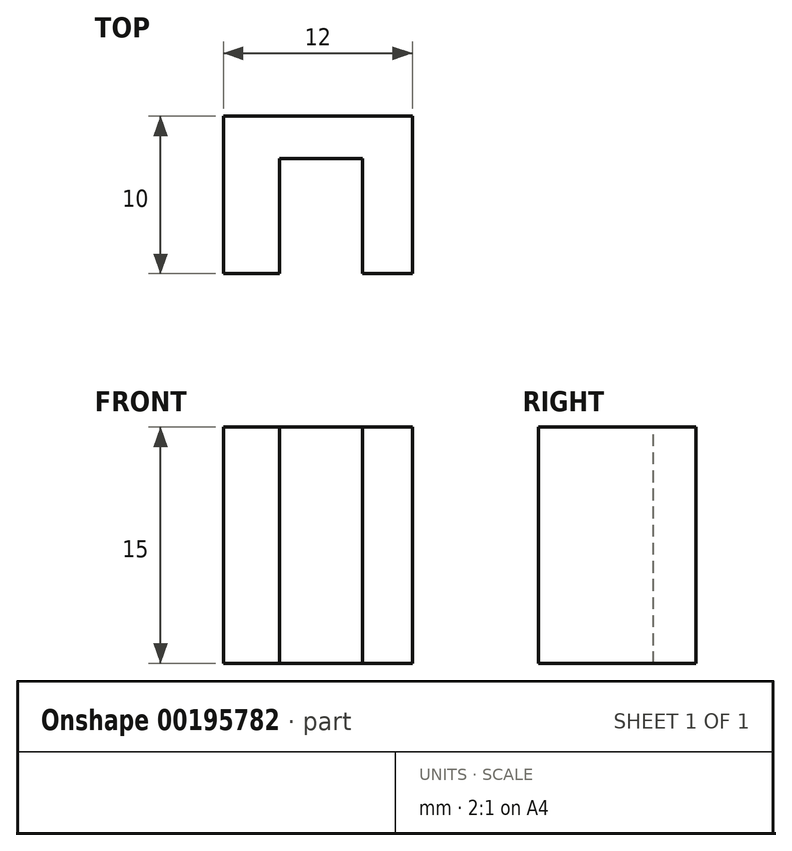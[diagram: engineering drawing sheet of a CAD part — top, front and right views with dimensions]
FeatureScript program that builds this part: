
annotation { "Feature Type Name" : "Feature", "Feature Type Description" : "" }
export const myFeature = defineFeature(function(context is Context, id is Id, definition is map)
    precondition{}
    {
        {
            var Q0;
            Q0=qCreatedBy(makeId("Top.planeOp"),FACE);
            var sketch = newSketch(context, id + "F0", { "sketchPlane" : qUnion([Q0])});
            skLineSegment(sketch, "E0.bottom", {"start": v(-11.4, 5.66) * mm, "end": v(0.6, 5.66) * mm});
            skLineSegment(sketch, "E0.top", {"start": v(-11.4, -4.34) * mm, "end": v(0.6, -4.34) * mm});
            skLineSegment(sketch, "E0.left", {"start": v(-11.4, 5.66) * mm, "end": v(-11.4, -4.34) * mm});
            skLineSegment(sketch, "E0.right", {"start": v(0.6, 5.66) * mm, "end": v(0.6, -4.34) * mm});
            skSolve(sketch);
        }
        {
            var Q0;
            Q0 = qSketchRegion(id + "F0", true);
            extrude(context, id + "F1", {"entities" : qUnion([Q0]), "depth" : 15 * mm});
        }
        {
            var Q0;
            Q0=makeQuery(id+"F1.opExtrude","CAP_FACE",FACE,{"disambiguationData":[OSD([sQuery(id+"F0.wireOp",EDGE,"E0.bottom"),sQuery(id+"F0.wireOp",EDGE,"E0.top"),sQuery(id+"F0.wireOp",EDGE,"E0.left"),sQuery(id+"F0.wireOp",EDGE,"E0.right")])],"isStart":false});
            var sketch = newSketch(context, id + "F2", { "sketchPlane" : qUnion([Q0])});
            skLineSegment(sketch, "E1.bottom", {"start": v(-7.83, -4.34) * mm, "end": v(-2.56, -4.34) * mm});
            skLineSegment(sketch, "E1.top", {"start": v(-7.83, 2.97) * mm, "end": v(-2.56, 2.97) * mm});
            skLineSegment(sketch, "E1.left", {"start": v(-7.83, -4.34) * mm, "end": v(-7.83, 2.97) * mm});
            skLineSegment(sketch, "E1.right", {"start": v(-2.56, -4.34) * mm, "end": v(-2.56, 2.97) * mm});
            skSolve(sketch);
        }
        {
            var Q0;
            Q0 = qSketchRegion(id + "F2", true);
            extrude(context, id + "F3", {"entities" : qUnion([Q0]), "operationType" : NewBodyOperationType.REMOVE, "endBound" : BoundingType.THROUGH_ALL, "oppositeDirection" : true, "depth" : 25 * mm});
        }
    });
